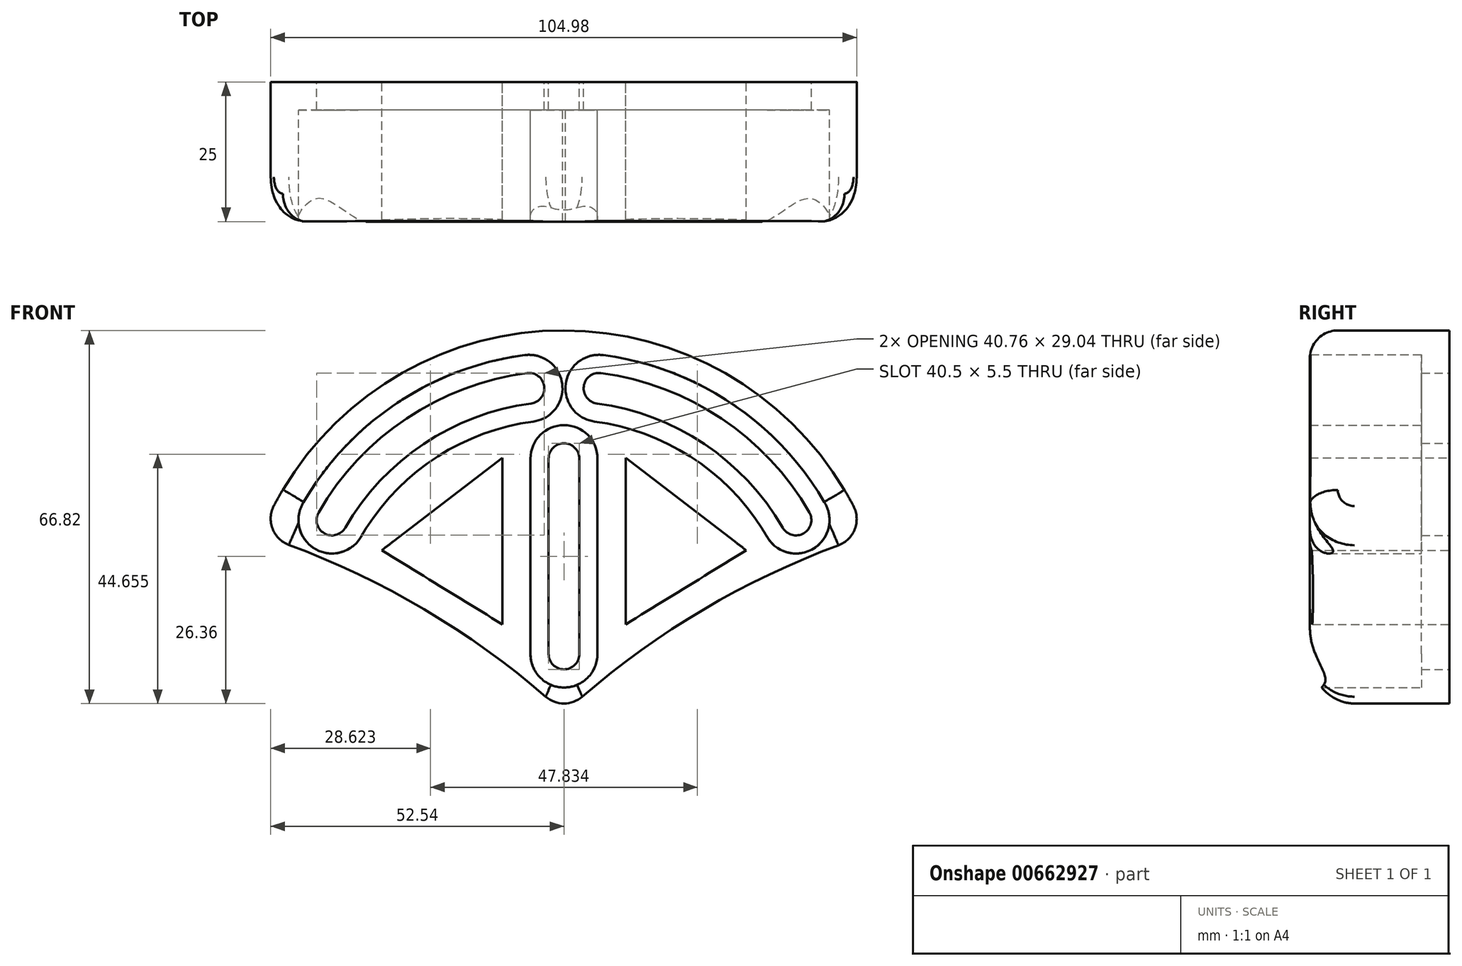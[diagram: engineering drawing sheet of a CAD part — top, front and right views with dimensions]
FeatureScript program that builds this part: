
annotation { "Feature Type Name" : "Feature", "Feature Type Description" : "" }
export const myFeature = defineFeature(function(context is Context, id is Id, definition is map)
    precondition{}
    {
        {
            var Q0;
            Q0=qCreatedBy(makeId("Front.planeOp"),FACE);
            var sketch = newSketch(context, id + "F0", { "sketchPlane" : qUnion([Q0])});
            skArc(sketch, "E0", {"start": v(2.75, 35) * mm, "mid": v(0, 37.75) * mm, "end": v(-2.75, 35) * mm});
            skArc(sketch, "E1", {"start": v(6, 35) * mm, "mid": v(0, 41) * mm, "end": v(-6, 35) * mm});
            skLineSegment(sketch, "E2", {"start": v(6, 0) * mm, "end": v(6, 35) * mm});
            skLineSegment(sketch, "E3", {"start": v(-6, 0) * mm, "end": v(-6, 35) * mm});
            skArc(sketch, "E4", {"start": v(-5.9, 44.86) * mm, "mid": v(-3.54, 47.95) * mm, "end": v(-6.62, 50.32) * mm});
            skArc(sketch, "E5", {"start": v(-43.95, 25.37) * mm, "mid": v(-42.94, 21.62) * mm, "end": v(-39.19, 22.62) * mm});
            skArc(sketch, "E6", {"start": v(-46.77, 27) * mm, "mid": v(-44.57, 18.8) * mm, "end": v(-36.37, 21) * mm});
            skArc(sketch, "E7", {"start": v(36.37, 21) * mm, "mid": v(23.33, 34.92) * mm, "end": v(5.48, 41.64) * mm});
            skArc(sketch, "E8", {"start": v(46.77, 27) * mm, "mid": v(30, 44.9) * mm, "end": v(7.05, 53.54) * mm});
            skArc(sketch, "E9.MirrorC", {"start": v(5.9, 44.86) * mm, "mid": v(3.54, 47.95) * mm, "end": v(6.62, 50.32) * mm});
            skArc(sketch, "E10.MirrorC", {"start": v(5.48, 41.64) * mm, "mid": v(0.32, 48.37) * mm, "end": v(7.05, 53.54) * mm});
            skArc(sketch, "E11.MirrorC", {"start": v(43.95, 25.37) * mm, "mid": v(42.94, 21.62) * mm, "end": v(39.19, 22.62) * mm});
            skArc(sketch, "E12.MirrorC", {"start": v(46.77, 27) * mm, "mid": v(44.57, 18.8) * mm, "end": v(36.37, 21) * mm});
            skLineSegment(sketch, "E13", {"start": v(0, 0) * mm, "end": v(0, -10.55) * mm, "construction": true});
            skArc(sketch, "E14.trimOffspring", {"start": v(-5.48, 41.64) * mm, "mid": v(-23.33, 34.92) * mm, "end": v(-36.37, 21) * mm});
            skArc(sketch, "E15.trimOffspring", {"start": v(-7.05, 53.54) * mm, "mid": v(-30, 44.9) * mm, "end": v(-46.77, 27) * mm});
            skLineSegment(sketch, "E16", {"start": v(41.57, 24) * mm, "end": v(47.38, 22.5) * mm, "construction": true});
            skArc(sketch, "E17", {"start": v(39.19, 22.62) * mm, "mid": v(25.14, 37.62) * mm, "end": v(5.9, 44.86) * mm});
            skArc(sketch, "E18", {"start": v(43.95, 25.37) * mm, "mid": v(28.2, 42.2) * mm, "end": v(6.62, 50.32) * mm});
            skArc(sketch, "E19.trimOffspring", {"start": v(-6.62, 50.32) * mm, "mid": v(-28.2, 42.2) * mm, "end": v(-43.95, 25.37) * mm});
            skArc(sketch, "E20.trimOffspring", {"start": v(-5.9, 44.86) * mm, "mid": v(-25.14, 37.62) * mm, "end": v(-39.19, 22.62) * mm});
            skArc(sketch, "E21.trimOffspring", {"start": v(-5.48, 41.64) * mm, "mid": v(-0.32, 48.37) * mm, "end": v(-7.05, 53.54) * mm});
            skLineSegment(sketch, "E22", {"start": v(2.75, 0) * mm, "end": v(2.75, 35) * mm});
            skLineSegment(sketch, "E23", {"start": v(-2.75, 35) * mm, "end": v(-2.75, 0) * mm});
            skArc(sketch, "E24.trimOffspring", {"start": v(-2.75, 0) * mm, "mid": v(0, -2.75) * mm, "end": v(2.75, 0) * mm});
            skArc(sketch, "E25.trimOffspring", {"start": v(-6, 0) * mm, "mid": v(0, -6) * mm, "end": v(6, 0) * mm});
            skArc(sketch, "E26", {"start": v(0, -10.55) * mm, "mid": v(-25.5, 8.28) * mm, "end": v(-54.38, 21.34) * mm});
            skArc(sketch, "E27", {"start": v(54.27, 21.27) * mm, "mid": v(25.45, 8.23) * mm, "end": v(0, -10.55) * mm});
            skPoint(sketch, "E28.MirrorCS.end.orphan", {"position": v(0, -10.55) * mm});
            skLineSegment(sketch, "E29", {"start": v(-32.64, 18.58) * mm, "end": v(-11.04, 5.31) * mm});
            skLineSegment(sketch, "E30", {"start": v(-11.04, 5.31) * mm, "end": v(-11.04, 35.14) * mm});
            skLineSegment(sketch, "E31", {"start": v(-11.04, 35.14) * mm, "end": v(-32.64, 18.58) * mm});
            skLineSegment(sketch, "E32.MirrorCS", {"start": v(11.04, 5.31) * mm, "end": v(11.04, 35.14) * mm});
            skLineSegment(sketch, "E33.MirrorCS", {"start": v(32.64, 18.58) * mm, "end": v(11.04, 5.31) * mm});
            skLineSegment(sketch, "E34.MirrorCS", {"start": v(11.04, 35.14) * mm, "end": v(32.64, 18.58) * mm});
            skArc(sketch, "E35", {"start": v(54.27, 21.27) * mm, "mid": v(-0.03, 57.96) * mm, "end": v(-54.38, 21.34) * mm});
            skSolve(sketch);
        }
        {
            var Q0;
            Q0 = qSketchRegion(id + "F0", true);
            extrude(context, id + "F1", {"entities" : qUnion([Q0]), "depth" : 25 * mm, "offsetDistance" : 25 * mm});
        }
        {
            var Q0;
            Q0=makeQuery(id+"F0.imprint","IMPRINT",FACE,{"disambiguationData":[TD([[makeQuery(id+"F0.imprint","IMPRINT",EDGE,{"derivedFrom":sQuery(id+"F0.wireOp",EDGE,"E4")}),-1.0]])]});
            var Q1;
            Q1=makeQuery(id+"F0.imprint","IMPRINT",FACE,{"disambiguationData":[TD([[makeQuery(id+"F0.imprint","IMPRINT",EDGE,{"derivedFrom":sQuery(id+"F0.wireOp",EDGE,"E7")}),-1.0]])]});
            var Q2;
            Q2=makeQuery(id+"F0.imprint","IMPRINT",FACE,{"disambiguationData":[TD([[makeQuery(id+"F0.imprint","IMPRINT",EDGE,{"derivedFrom":sQuery(id+"F0.wireOp",EDGE,"E0")}),-1.0]])]});
            extrude(context, id + "F2", {"entities" : qUnion([Q0, Q1, Q2]), "operationType" : NewBodyOperationType.ADD, "depth" : 5 * mm, "offsetDistance" : 25 * mm});
        }
        {
            var Q0;
            Q0=makeQuery(id+"F1.opExtrude","CAP_EDGE",EDGE,{"disambiguationData":[OSD([sQuery(id+"F0.wireOp",EDGE,"7b9ec517-82f2-4ae6-85a2-77c8b9b1b1412")])],"isStart":false});
            var Q1;
            Q1=makeQuery(id+"F1.opExtrude","CAP_EDGE",EDGE,{"disambiguationData":[OSD([sQuery(id+"F0.wireOp",EDGE,"E26")])],"isStart":false});
            var Q2;
            Q2=makeQuery(id+"F1.opExtrude","CAP_EDGE",EDGE,{"disambiguationData":[OSD([sQuery(id+"F0.wireOp",EDGE,"E27")])],"isStart":false});
            fillet(context, id + "F3", {"entities" : qUnion([Q0, Q1, Q2]), "radius" : 8 * mm, "tangentPropagation" : true, "allowEdgeOverflow" : false});
        }
        {
            var Q0;
            Q0=makeQuery(id+"F1.opExtrude","SWEPT_EDGE",EDGE,{"disambiguationData":[OSD([sQuery(id+"F0.wireOp",EDGE,"7b9ec517-82f2-4ae6-85a2-77c8b9b1b1412"),sQuery(id+"F0.wireOp",EDGE,"E26")])]});
            var Q1;
            Q1=makeQuery(id+"F1.opExtrude","SWEPT_EDGE",EDGE,{"disambiguationData":[OSD([sQuery(id+"F0.wireOp",EDGE,"E26"),sQuery(id+"F0.wireOp",EDGE,"E27")])]});
            var Q2;
            Q2=makeQuery(id+"F1.opExtrude","SWEPT_EDGE",EDGE,{"disambiguationData":[OSD([sQuery(id+"F0.wireOp",EDGE,"7b9ec517-82f2-4ae6-85a2-77c8b9b1b1412"),sQuery(id+"F0.wireOp",EDGE,"E27")])]});
            fillet(context, id + "F4", {"entities" : qUnion([Q0, Q1, Q2]), "radius" : 5 * mm, "tangentPropagation" : true, "allowEdgeOverflow" : false});
        }
    });
